# Revit family: P200635WX-111c_WRF767SDH_VZ
name_source: partatom
category: Specialty Equipment
units: mm (PartAtom-declared; Revit-internal decimal feet)

## family parameters
Always vertical = Yes
Cut with Voids When Loaded = No
Enable Cutting in Views = No
Maintain Annotation Orientation = No
Part Type = Normal
Room Calculation Point = No
Round Connector Dimension = Use Diameter
Shared = No
Work Plane-Based = No

## types (2) — shared parameters
Amps = 0 A
Clearance Material = ARCAT - Clearance
Default Elevation = 0"
Depth = 35 5/8"
Description = 36-inch Wide French Door Refrigerator - 27 cu. ft.
Réfrigérateur à portes françaises, 36 po, 27 pi³
Dimension Guide = http://access.whirlpool.com Guide&sku=WRF767SDHV&language=EN
http://access.whirlpool.com Guide&sku=WRF767SDHV&language=EN
Display Panel Material = ARCAT - Metal - Steel - Black
Energy Guide = http://access.whirlpool.com Guide&sku=WRF767SDHV&language=EN
http://access.whirlpool.com Guide&sku=WRF767SDHV&language=FR
Family Name = French Door Bottom Mount
Feature 1 = Platter Pocket
Casier à plateaux
Feature 2 = Fingerprint Resistant
Acier inoxydable résistant aux traces de doigts
Feature 3 = In-Door-Ice® Storage
Machine à glaçons dans la porte In-Door-Ice®
Height = 69 7/8"
Manufacturer = Whirlpool
Voltage = 0 V
Width = 35 11/16"

## per-type parameters (varying)
| type | Accent Material | Body Material | Door Material | Handle Material |
| WRF767SDHZ | ARCAT - Metal - Steel -Gray | ARCAT - Metal - Steel -Gray | ARCAT - Metal - Steel - Stainless | ARCAT - Metal - Steel -Gray - Light |
| WRF767SDHV | ARCAT - Metal - Steel - Black - Light | ARCAT - Metal - Steel - Black - Light | ARCAT - Metal - Steel - Stainless - Black | ARCAT - Metal - Steel - Stainless - Grey |

note: column(s) folded — value = type name in every type: Model

## geometry (parser evidence)
native form markers: Sweep x5
no freeform markers — native parametric forms only
